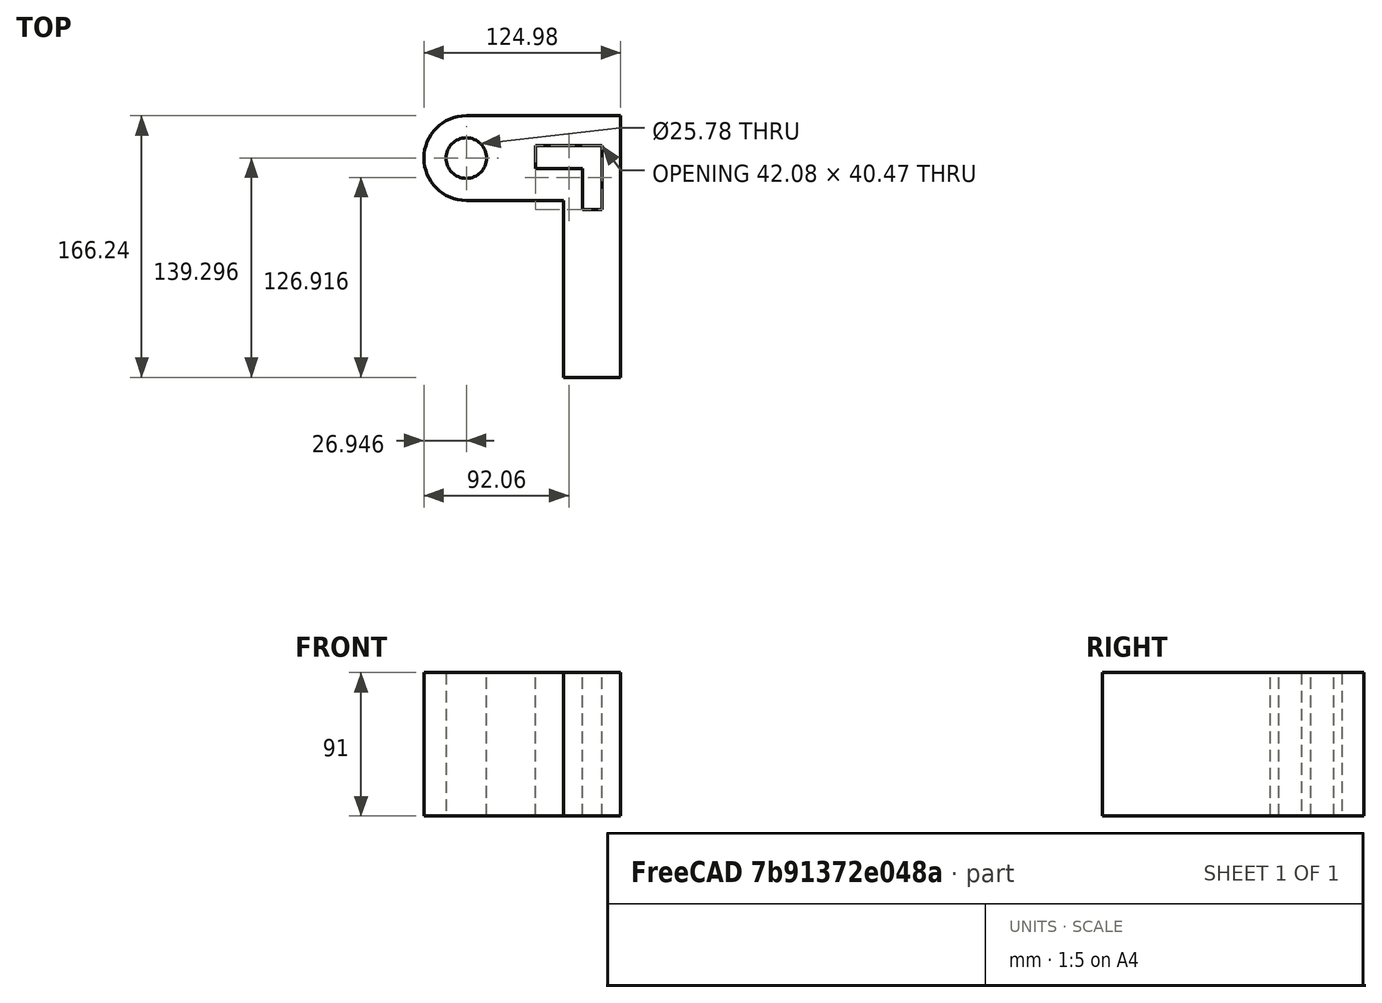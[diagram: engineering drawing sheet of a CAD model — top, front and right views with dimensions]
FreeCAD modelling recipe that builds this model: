
FCSTD DOCUMENT  (FreeCAD 0.19R17171 (Git))
Label: Fem
License: CC-BY 3.0
LicenseURL: http://creativecommons.org/licenses/by/3.0/
objects: Sketcher::SketchObject×1, PartDesign::Pad×1, Fem::FemMeshShapeObject×1, Fem::ConstraintFixed×1, Fem::ConstraintForce×1
note: 3 computed .brp shape members not serialized (recipe doc carries the construction recipe); baked Part::Feature solids carry a one-line shape summary decoded from their .brp

FEATURE [Sketcher::SketchObject] Sketch
  MapMode = 5
  sketch-geometry (13):
    g0: ArcOfCircle CenterX=-29.9237 CenterY=19.9863 CenterZ=0 NormalX=0 NormalY=0 NormalZ=1 AngleXU=0 Radius=26.9466 StartAngle=1.5708 EndAngle=4.71239
    g1: LineSegment StartX=-29.9237 StartY=46.933 StartZ=0 EndX=68.1073 EndY=46.933 EndZ=0
    g2: LineSegment StartX=68.1073 StartY=46.933 StartZ=0 EndX=68.1073 EndY=-119.309 EndZ=0
    g3: LineSegment StartX=68.1073 StartY=-119.309 StartZ=0 EndX=31.7141 EndY=-119.309 EndZ=0
    g4: LineSegment StartX=31.7141 StartY=-119.309 StartZ=0 EndX=31.7141 EndY=-6.96029 EndZ=0
    g5: LineSegment StartX=31.7141 StartY=-6.96029 StartZ=0 EndX=-29.9236 EndY=-6.96029 EndZ=0
    g6: Circle CenterX=-29.9237 CenterY=19.9863 CenterZ=0 NormalX=0 NormalY=0 NormalZ=1 AngleXU=0 Radius=12.8881
    g7: LineSegment StartX=14.1478 StartY=27.839 StartZ=0 EndX=56.2317 EndY=27.839 EndZ=0
    g8: LineSegment StartX=56.2317 StartY=27.839 StartZ=0 EndX=56.2317 EndY=-12.6263 EndZ=0
    g9: LineSegment StartX=56.2317 StartY=-12.6263 StartZ=0 EndX=43.9303 EndY=-12.6263 EndZ=0
    g10: LineSegment StartX=43.9303 StartY=-12.6263 StartZ=0 EndX=43.9303 EndY=13.2715 EndZ=0
    g11: LineSegment StartX=43.9303 StartY=13.2715 StartZ=0 EndX=14.1478 EndY=13.2715 EndZ=0
    g12: LineSegment StartX=14.1478 StartY=13.2715 StartZ=0 EndX=14.1478 EndY=27.839 EndZ=0
  constraints (25):
    c: Tangent(g0,g1)
    c: Coincident(g1,g2)
    c: Vertical(g2)
    c: Coincident(g2,g3)
    c: Horizontal(g3)
    c: Coincident(g3,g4)
    c: Vertical(g4)
    c: Coincident(g4,g5)
    c: Coincident(g5,g0)
    c: Horizontal(g5)
    c: Horizontal(g1)
    c: Tangent(g0,g5)
    c: Coincident(g6,g0)
    c: Horizontal(g7)
    c: Coincident(g7,g8)
    c: Vertical(g8)
    c: Coincident(g8,g9)
    c: Horizontal(g9)
    c: Coincident(g9,g10)
    c: Vertical(g10)
    c: Coincident(g10,g11)
    c: Horizontal(g11)
    c: Coincident(g11,g12)
    c: Coincident(g12,g7)
    c: Vertical(g12)
FEATURE [PartDesign::Pad] Pad
  Length = 91
  Length2 = 100
  Profile = -> Sketch
  Type = 0
FEATURE [Fem::FemMeshShapeObject] FemShape
  Shape = -> Pad
FEATURE [Fem::ConstraintFixed] FemConstraintFixed
  NormalDirection = (0,-1,0)
  Normals = (16) [(0,-1,0),(0,-1,0),(0,-1,0),(0,-1,0),(0,-1,0),(0,-1,0),(0,-1,0),(0,-1,0),(0,-1,0),(0,-1,0),(0,-1,0),(0,-1,0),(0,-1,0),(0,-1,0),(0,-1,0),(0,-1,0)]
  Points = (16) [(68.1073,-119.309,91),(55.9762,-119.309,91),(43.8452,-119.309,91),(31.7141,-119.309,91),(68.1073,-119.309,60.6667),(55.9762,-119.309,60.6667),+10 more]
  References = -> [Pad]
  Scale = 7
FEATURE [Fem::ConstraintForce] FemConstraintForce
  DirectionVector = (-1,-2.3988e-07,0)
  Force = 0
  NormalDirection = (-1,-2.3988e-07,0)
  Points = (16) [(-29.9237,46.933,91),(-53.2601,33.4596,91),(-53.2601,6.51301,91),(-29.9236,-6.96029,91),(-29.9237,46.933,60.6667),(-53.2601,33.4596,60.6667),+10 more]
  References = -> [Pad]
  Scale = 9
